# Revit family: xRobe_Hook-American_Standard-Studio_S-7105.210
name_source: partatom
category: Specialty Equipment
revit_build: Autodesk Revit 2014 (Build: 20130308_1515(x64)
units: mm (PartAtom-declared; Revit-internal decimal feet)

## types (1)
- 7105.210
    Assembly Code = C1030220
    Default Elevation = 60"
    Description = Studio S Bath Accessories Robe Hook
    Finish = Metal-American Standard-002-Polished Chrome
    Height = 4 1/16"
    Installation Type = Wall Mount
    Length = 1 5/8"
    Manufacturer = American Standard
    Material = Metal-American Standard-002-Polished Chrome
    Model = 7105.210
    Price = Prices may vary. Please consult Manufacturer Representative for most up-to-date price list.
    Product Documentation Link = https://www.americanstandard-us.com
    Product Page URL = https://www.americanstandard-us.com
    Specification = Robe Hook shall feature metal construction. Shall feature concealed mounting with no exposed set screws. Robe Hook shall be American Standard Model 7105.210
    URL = https://www.americanstandard-us.com
    Warranty Information = One Year General Product Warranty
    Width = 2 15/16"

## geometry (parser evidence)
native form markers: Sweep x2
no freeform markers — native parametric forms only
